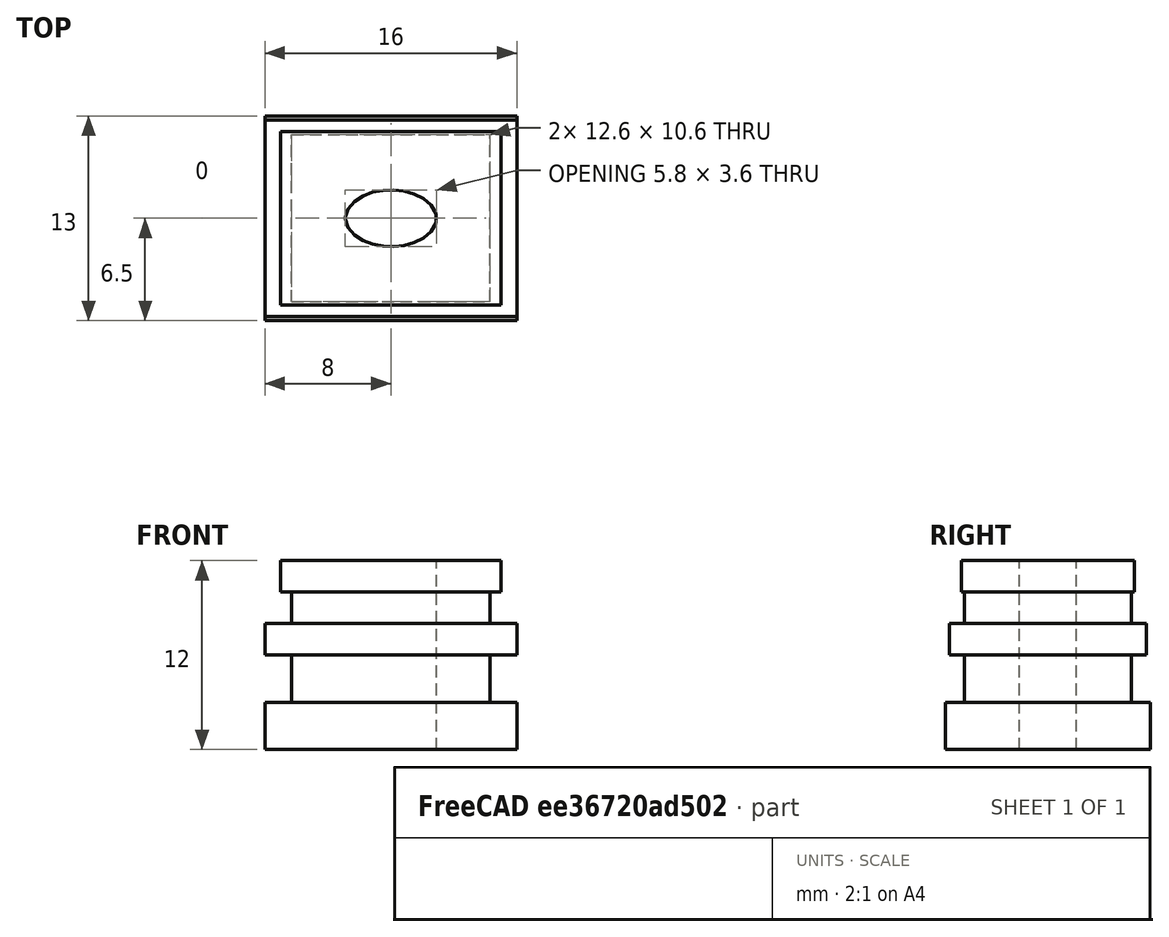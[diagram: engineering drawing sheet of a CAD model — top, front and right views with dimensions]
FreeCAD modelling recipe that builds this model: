
FCSTD DOCUMENT  (FreeCAD 0.19R0.19.2)
Label: 03
License: All rights reserved
LicenseURL: http://en.wikipedia.org/wiki/All_rights_reserved
objects: Part::Box×5, Sketcher::SketchObject×3, Part::MultiFuse×1, Part::Extrusion×1, Part::Cut×1
note: 11 computed .brp shape members not serialized (recipe doc carries the construction recipe); baked Part::Feature solids carry a one-line shape summary decoded from their .brp

FEATURE [Sketcher::SketchObject] Sketch
  FullyConstrained = true
FEATURE [Part::Box] Box  label="Cube"
  AttacherType = Attacher::AttachEngine3D
  Height = 3
  Length = 12.6
  Placement = pos=(1.7,1.2,3) rot=(0,0,1;0rad)
  Width = 10.6
FEATURE [Part::Box] Box001  label="Cube001"
  AttacherType = Attacher::AttachEngine3D
  Height = 3
  Length = 16
  Width = 13
FEATURE [Part::Box] Box002  label="Cube002"
  AttacherType = Attacher::AttachEngine3D
  Height = 2
  Length = 16
  Placement = pos=(0,0.25,6) rot=(0,0,1;0rad)
  Width = 12.5
FEATURE [Part::Box] Box003  label="Cube003"
  AttacherType = Attacher::AttachEngine3D
  Height = 2
  Length = 12.6
  Placement = pos=(1.7,1.2,8) rot=(0,0,1;0rad)
  Width = 10.6
FEATURE [Part::Box] Box004  label="Cube004"
  AttacherType = Attacher::AttachEngine3D
  Height = 2
  Length = 14
  Placement = pos=(1,1,10) rot=(0,0,1;0rad)
  Width = 11
FEATURE [Part::MultiFuse] Fusion
  Shapes = -> [Box004,Box003,Box002,Box,Box001]
FEATURE [Sketcher::SketchObject] Sketch001
  FullyConstrained = true
  MapMode = 5
  Placement = pos=(0,0,12) rot=(0,0,1;0rad)
  Support = -> [Fusion]
FEATURE [Sketcher::SketchObject] Sketch002
  FullyConstrained = true
  MapMode = 5
  Placement = pos=(0,0,12) rot=(0,0,1;0rad)
  Support = -> [Fusion]
  sketch-geometry (5):
    g0: Ellipse CenterX=1e-16 CenterY=0 CenterZ=0 NormalX=0 NormalY=0 NormalZ=1 MajorRadius=2.9 MinorRadius=1.8 AngleXU=-3.14159
    g1: LineSegment StartX=-2.9 StartY=0 StartZ=0 EndX=2.9 EndY=0 EndZ=0
    g2: LineSegment StartX=1e-16 StartY=-1.8 StartZ=0 EndX=1e-16 EndY=1.8 EndZ=0
    g3: GeomPoint X=-2.27376 Y=0 Z=0
    g4: GeomPoint X=2.27376 Y=0 Z=0
  constraints (2):
    c: InternalAlignment(g1-g4 -> g0) x4
    c: Block(g0)
FEATURE [Part::Extrusion] Extrude
  Base = -> Sketch002
  Dir = (0,0,1)
  DirMode = 2
  FaceMakerClass = Part::FaceMakerBullseye
  LengthFwd = 14
  LengthRev = 0
  Placement = pos=(8,6.5,-13) rot=(0,0,1;0rad)
  Solid = true
  Symmetric = false
FEATURE [Part::Cut] Cut
  Base = -> Fusion
  Tool = -> Extrude
